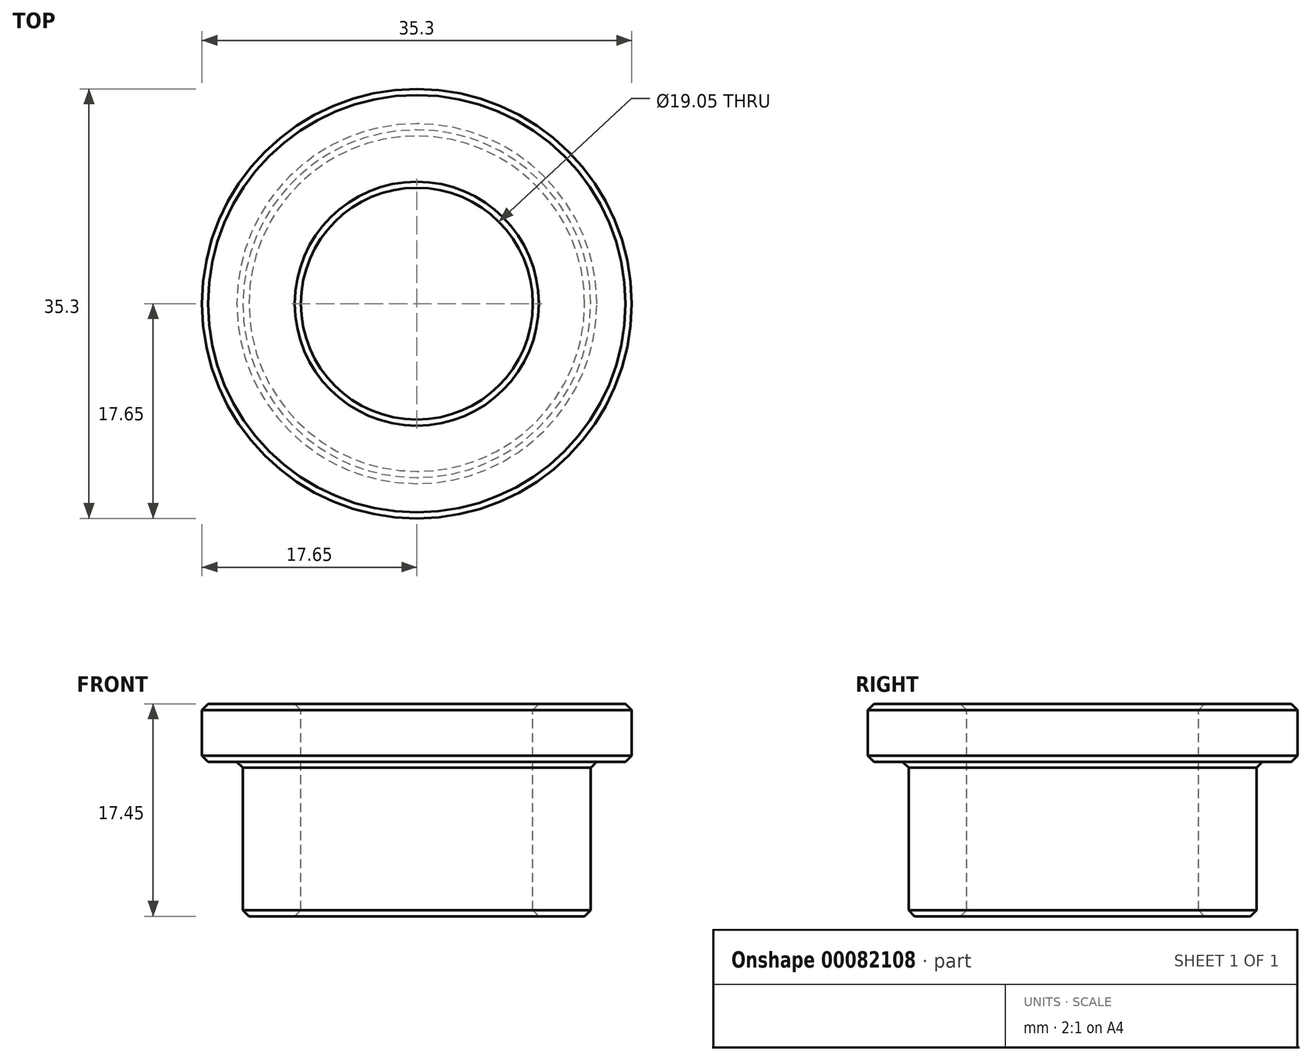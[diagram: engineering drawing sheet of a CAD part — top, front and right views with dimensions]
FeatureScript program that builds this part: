
annotation { "Feature Type Name" : "Feature", "Feature Type Description" : "" }
export const myFeature = defineFeature(function(context is Context, id is Id, definition is map)
    precondition{}
    {
        {
            var Q0;
            Q0=qCreatedBy(makeId("Top.planeOp"),FACE);
            var sketch = newSketch(context, id + "F0", { "sketchPlane" : qUnion([Q0])});
            skCircle(sketch, "E0", {"center": v(0, 0) * mm, "radius": 14.29 * mm});
            skCircle(sketch, "E1", {"center": v(0, 0) * mm, "radius": 9.53 * mm});
            skSolve(sketch);
        }
        {
            var Q0;
            Q0=makeQuery(id+"F0.imprint","IMPRINT",FACE,{"disambiguationData":[TD([[makeQuery(id+"F0.imprint","IMPRINT",EDGE,{"derivedFrom":sQuery(id+"F0.wireOp",EDGE,"E0")}),1.0]])]});
            extrude(context, id + "F1", {"entities" : qUnion([Q0]), "oppositeDirection" : true, "depth" : 12.7 * mm});
        }
        {
            var Q0;
            Q0=qCreatedBy(makeId("Top.planeOp"),FACE);
            var sketch = newSketch(context, id + "F2", { "sketchPlane" : qUnion([Q0])});
            skCircle(sketch, "E2.0", {"center": v(0, 0) * mm, "radius": 9.53 * mm});
            skCircle(sketch, "E3", {"center": v(0, 0) * mm, "radius": 17.65 * mm});
            skSolve(sketch);
        }
        {
            var Q0;
            Q0 = qSketchRegion(id + "F2", true);
            extrude(context, id + "F3", {"entities" : qUnion([Q0]), "operationType" : NewBodyOperationType.ADD, "depth" : 4.75 * mm});
        }
        {
            var Q0;
            Q0=makeQuery(id+"F3.opExtrude","SWEPT_FACE",FACE,{"disambiguationData":[OSD([sQuery(id+"F2.wireOp",EDGE,"E3")])]});
            var Q1;
            Q1=makeQuery(id+"F3.boolean.opBoolean","MERGE",FACE,{"derivedFrom":[makeQuery(id+"F1.opExtrude","SWEPT_FACE",FACE,{"disambiguationData":[OSD([sQuery(id+"F0.wireOp",EDGE,"E1")])]}),makeQuery(id+"F3.opExtrude","SWEPT_FACE",FACE,{"disambiguationData":[OSD([sQuery(id+"F2.wireOp",EDGE,"E2.0")])]})]});
            var Q2;
            Q2=makeQuery(id+"F1.opExtrude","SWEPT_FACE",FACE,{"disambiguationData":[OSD([sQuery(id+"F0.wireOp",EDGE,"E0")])]});
            chamfer(context, id + "F4", {"entities" : qUnion([Q0, Q1, Q2]), "width" : 0.5 * mm, "tangentPropagation" : true});
        }
    });
